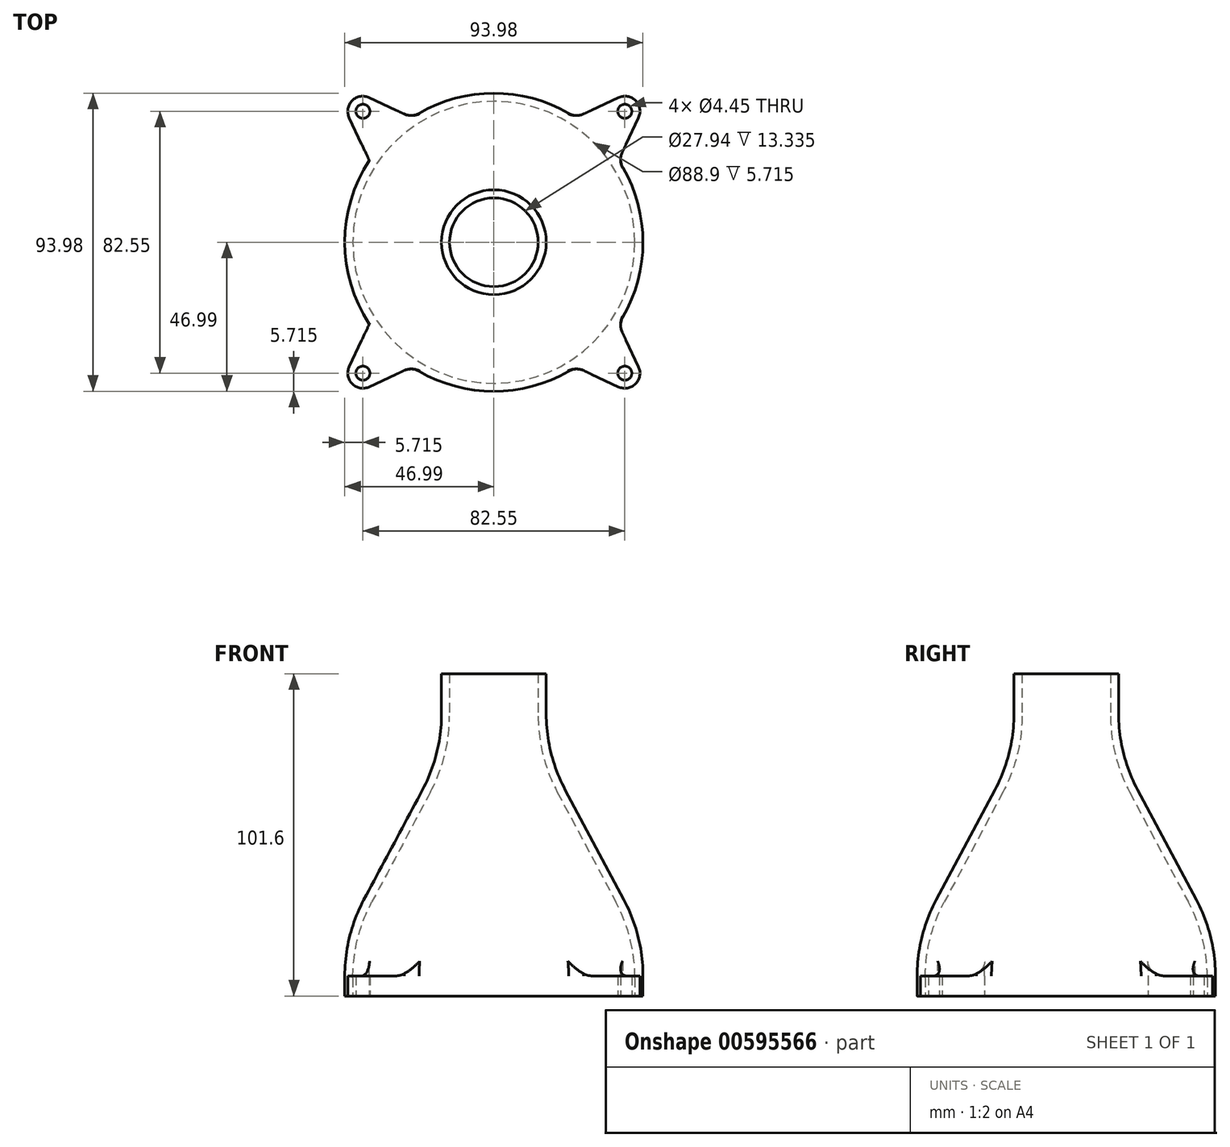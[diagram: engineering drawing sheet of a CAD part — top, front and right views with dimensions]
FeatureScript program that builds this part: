
annotation { "Feature Type Name" : "Feature", "Feature Type Description" : "" }
export const myFeature = defineFeature(function(context is Context, id is Id, definition is map)
    precondition{}
    {
        {
            var Q0;
            Q0=qCreatedBy(makeId("Front.planeOp"),FACE);
            var sketch = newSketch(context, id + "F0", { "sketchPlane" : qUnion([Q0])});
            skLineSegment(sketch, "E0", {"start": v(-66.35, 101.6) * mm, "end": v(86.52, 101.6) * mm, "construction": true});
            skLineSegment(sketch, "E1", {"start": v(0, 0) * mm, "end": v(0, 101.6) * mm, "construction": true});
            skLineSegment(sketch, "E2", {"start": v(-16.51, 101.6) * mm, "end": v(-16.51, 88.9) * mm});
            skLineSegment(sketch, "E3", {"start": v(-22.49, 65) * mm, "end": v(-41.01, 30.26) * mm});
            skLineSegment(sketch, "E4", {"start": v(-46.99, 6.35) * mm, "end": v(-46.99, 0) * mm});
            skLineSegment(sketch, "E5", {"start": v(-46.99, 0) * mm, "end": v(-44.45, 0) * mm});
            skLineSegment(sketch, "E6", {"start": v(-44.45, 0) * mm, "end": v(-44.45, 5.71) * mm});
            skLineSegment(sketch, "E7", {"start": v(-38.47, 29.62) * mm, "end": v(-19.95, 64.36) * mm});
            skLineSegment(sketch, "E8", {"start": v(-13.97, 88.27) * mm, "end": v(-13.97, 101.6) * mm});
            skLineSegment(sketch, "E9", {"start": v(-13.97, 101.6) * mm, "end": v(-16.51, 101.6) * mm});
            skPoint(sketch, "E10.visualSharp", {"position": v(-16.51, 76.2) * mm});
            skArc(sketch, "E10.filletArc", {"start": v(-22.49, 65) * mm, "mid": v(-18.03, 76.58) * mm, "end": v(-16.5, 88.9) * mm});
            skPoint(sketch, "E11.visualSharp", {"position": v(-13.97, 75.57) * mm});
            skArc(sketch, "E11.filletArc", {"start": v(-19.95, 64.36) * mm, "mid": v(-15.49, 75.94) * mm, "end": v(-13.97, 88.27) * mm});
            skPoint(sketch, "E12.visualSharp", {"position": v(-44.45, 18.42) * mm});
            skArc(sketch, "E12.filletArc", {"start": v(-38.47, 29.62) * mm, "mid": v(-42.93, 18.04) * mm, "end": v(-44.45, 5.71) * mm});
            skPoint(sketch, "E13.visualSharp", {"position": v(-47, 19.05) * mm});
            skArc(sketch, "E13.filletArc", {"start": v(-41.01, 30.26) * mm, "mid": v(-45.47, 18.67) * mm, "end": v(-46.99, 6.35) * mm});
            skSolve(sketch);
        }
        {
            var Q0;
            Q0=makeQuery(id+"F0.imprint","IMPRINT",FACE,{"disambiguationData":[TD([[makeQuery(id+"F0.imprint","IMPRINT",EDGE,{"derivedFrom":sQuery(id+"F0.wireOp",EDGE,"E2")}),1.0]])]});
            var Q1;
            Q1=sQuery(id+"F0.wireOp",EDGE,"E1");
            revolve(context, id + "F1", {"entities" : qUnion([Q0]), "axis" : qUnion([Q1]), "revolveType" : RevolveType.FULL});
        }
        {
            var Q0;
            Q0=qCreatedBy(makeId("Top.planeOp"),FACE);
            var sketch = newSketch(context, id + "F2", { "sketchPlane" : qUnion([Q0])});
            skLineSegment(sketch, "E14.bottom", {"start": v(-41.28, -41.28) * mm, "end": v(41.28, -41.28) * mm, "construction": true});
            skLineSegment(sketch, "E14.top", {"start": v(-41.27, 41.28) * mm, "end": v(41.28, 41.28) * mm, "construction": true});
            skLineSegment(sketch, "E14.left", {"start": v(-41.27, -41.28) * mm, "end": v(-41.27, 41.28) * mm, "construction": true});
            skLineSegment(sketch, "E14.right", {"start": v(41.28, -41.28) * mm, "end": v(41.28, 41.28) * mm, "construction": true});
            skLineSegment(sketch, "E15", {"start": v(-41.28, 41.28) * mm, "end": v(41.28, -41.28) * mm, "construction": true});
            skCircle(sketch, "E16", {"center": v(-41.28, -41.28) * mm, "radius": 2.22 * mm});
            skArc(sketch, "E17", {"start": v(-45.59, -39.25) * mm, "mid": v(-44.64, -44.64) * mm, "end": v(-39.25, -45.59) * mm});
            skLineSegment(sketch, "E18", {"start": v(-45.59, -39.25) * mm, "end": v(-39.27, -25.8) * mm});
            skLineSegment(sketch, "E19", {"start": v(-39.25, -45.59) * mm, "end": v(-25.8, -39.27) * mm});
            skArc(sketch, "E20.trimOffspring", {"start": v(-39.27, -25.8) * mm, "mid": v(-33.23, -33.23) * mm, "end": v(-25.8, -39.27) * mm});
            skLineSegment(sketch, "E21.1.0", {"start": v(39.25, -45.59) * mm, "end": v(25.8, -39.27) * mm});
            skCircle(sketch, "E21.1.1", {"center": v(41.28, -41.28) * mm, "radius": 2.22 * mm});
            skLineSegment(sketch, "E21.1.2", {"start": v(45.59, -39.25) * mm, "end": v(39.27, -25.8) * mm});
            skArc(sketch, "E21.1.3", {"start": v(39.25, -45.59) * mm, "mid": v(44.64, -44.64) * mm, "end": v(45.59, -39.25) * mm});
            skArc(sketch, "E21.1.4", {"start": v(25.8, -39.27) * mm, "mid": v(33.23, -33.23) * mm, "end": v(39.27, -25.8) * mm});
            skLineSegment(sketch, "E21.2.0", {"start": v(45.59, 39.25) * mm, "end": v(39.27, 25.8) * mm});
            skCircle(sketch, "E21.2.1", {"center": v(41.28, 41.27) * mm, "radius": 2.22 * mm});
            skLineSegment(sketch, "E21.2.2", {"start": v(39.25, 45.59) * mm, "end": v(25.8, 39.27) * mm});
            skArc(sketch, "E21.2.3", {"start": v(45.59, 39.25) * mm, "mid": v(44.64, 44.64) * mm, "end": v(39.25, 45.59) * mm});
            skArc(sketch, "E21.2.4", {"start": v(39.27, 25.8) * mm, "mid": v(33.23, 33.23) * mm, "end": v(25.8, 39.27) * mm});
            skLineSegment(sketch, "E21.3.0", {"start": v(-39.25, 45.59) * mm, "end": v(-25.8, 39.27) * mm});
            skCircle(sketch, "E21.3.1", {"center": v(-41.27, 41.28) * mm, "radius": 2.22 * mm});
            skLineSegment(sketch, "E21.3.2", {"start": v(-45.59, 39.25) * mm, "end": v(-39.27, 25.8) * mm});
            skArc(sketch, "E21.3.3", {"start": v(-39.25, 45.59) * mm, "mid": v(-44.64, 44.64) * mm, "end": v(-45.59, 39.25) * mm});
            skArc(sketch, "E21.3.4", {"start": v(-25.8, 39.27) * mm, "mid": v(-33.23, 33.23) * mm, "end": v(-39.27, 25.8) * mm});
            skSolve(sketch);
        }
        {
            var Q0;
            Q0=makeQuery(id+"F2.imprint","IMPRINT",FACE,{"disambiguationData":[TD([[makeQuery(id+"F2.imprint","IMPRINT",EDGE,{"derivedFrom":sQuery(id+"F2.wireOp",EDGE,"E16")}),-1.0]])]});
            var Q1;
            Q1=makeQuery(id+"F2.imprint","IMPRINT",FACE,{"disambiguationData":[TD([[makeQuery(id+"F2.imprint","IMPRINT",EDGE,{"derivedFrom":sQuery(id+"F2.wireOp",EDGE,"E21.1.0")}),-1.0]])]});
            var Q2;
            Q2=makeQuery(id+"F2.imprint","IMPRINT",FACE,{"disambiguationData":[TD([[makeQuery(id+"F2.imprint","IMPRINT",EDGE,{"derivedFrom":sQuery(id+"F2.wireOp",EDGE,"E21.2.0")}),-1.0]])]});
            var Q3;
            Q3=makeQuery(id+"F2.imprint","IMPRINT",FACE,{"disambiguationData":[TD([[makeQuery(id+"F2.imprint","IMPRINT",EDGE,{"derivedFrom":sQuery(id+"F2.wireOp",EDGE,"E21.3.0")}),-1.0]])]});
            extrude(context, id + "F3", {"entities" : qUnion([Q0, Q1, Q2, Q3]), "operationType" : NewBodyOperationType.ADD, "depth" : 6.35 * mm, "offsetDistance" : 25.4 * mm});
        }
        {
            var Q0;
            Q0=makeQuery(id+"F3.boolean.opBoolean","MERGE",EDGE,{"derivedFrom":[makeQuery(id+"F1.opRevolve","SWEPT_EDGE",EDGE,{"disambiguationData":[OSD([sQuery(id+"F0.wireOp",EDGE,"E4"),sQuery(id+"F0.wireOp",EDGE,"E13.filletArc")])]}),makeQuery(id+"F3.opExtrude","CAP_EDGE",EDGE,{"disambiguationData":[OSD([sQuery(id+"F2.wireOp",EDGE,"E20.trimOffspring")])],"isStart":false})]});
            var Q1;
            Q1=makeQuery(id+"F3.opExtrude","SWEPT_EDGE",EDGE,{"disambiguationData":[OSD([sQuery(id+"F2.wireOp",EDGE,"E19"),sQuery(id+"F2.wireOp",EDGE,"E20.trimOffspring")])]});
            var Q2;
            Q2=makeQuery(id+"F3.opExtrude","SWEPT_EDGE",EDGE,{"disambiguationData":[OSD([sQuery(id+"F2.wireOp",EDGE,"E18"),sQuery(id+"F2.wireOp",EDGE,"E20.trimOffspring")])]});
            var Q3;
            Q3=makeQuery(id+"F3.boolean.opBoolean","MERGE",EDGE,{"derivedFrom":[makeQuery(id+"F1.opRevolve","SWEPT_EDGE",EDGE,{"disambiguationData":[OSD([sQuery(id+"F0.wireOp",EDGE,"E4"),sQuery(id+"F0.wireOp",EDGE,"E13.filletArc")])]}),makeQuery(id+"F3.opExtrude","CAP_EDGE",EDGE,{"disambiguationData":[OSD([sQuery(id+"F2.wireOp",EDGE,"E21.3.4")])],"isStart":false})]});
            var Q4;
            Q4=makeQuery(id+"F3.opExtrude","SWEPT_EDGE",EDGE,{"disambiguationData":[OSD([sQuery(id+"F2.wireOp",EDGE,"E21.3.2"),sQuery(id+"F2.wireOp",EDGE,"E21.3.4")])]});
            var Q5;
            Q5=makeQuery(id+"F3.opExtrude","SWEPT_EDGE",EDGE,{"disambiguationData":[OSD([sQuery(id+"F2.wireOp",EDGE,"E21.3.0"),sQuery(id+"F2.wireOp",EDGE,"E21.3.4")])]});
            var Q6;
            Q6=makeQuery(id+"F3.opExtrude","SWEPT_EDGE",EDGE,{"disambiguationData":[OSD([sQuery(id+"F2.wireOp",EDGE,"E21.2.2"),sQuery(id+"F2.wireOp",EDGE,"E21.2.4")])]});
            var Q7;
            Q7=makeQuery(id+"F3.boolean.opBoolean","MERGE",EDGE,{"derivedFrom":[makeQuery(id+"F1.opRevolve","SWEPT_EDGE",EDGE,{"disambiguationData":[OSD([sQuery(id+"F0.wireOp",EDGE,"E4"),sQuery(id+"F0.wireOp",EDGE,"E13.filletArc")])]}),makeQuery(id+"F3.opExtrude","CAP_EDGE",EDGE,{"disambiguationData":[OSD([sQuery(id+"F2.wireOp",EDGE,"E21.2.4")])],"isStart":false})]});
            var Q8;
            Q8=makeQuery(id+"F3.opExtrude","SWEPT_EDGE",EDGE,{"disambiguationData":[OSD([sQuery(id+"F2.wireOp",EDGE,"E21.2.0"),sQuery(id+"F2.wireOp",EDGE,"E21.2.4")])]});
            var Q9;
            Q9=makeQuery(id+"F3.boolean.opBoolean","MERGE",EDGE,{"derivedFrom":[makeQuery(id+"F1.opRevolve","SWEPT_EDGE",EDGE,{"disambiguationData":[OSD([sQuery(id+"F0.wireOp",EDGE,"E4"),sQuery(id+"F0.wireOp",EDGE,"E13.filletArc")])]}),makeQuery(id+"F3.opExtrude","CAP_EDGE",EDGE,{"disambiguationData":[OSD([sQuery(id+"F2.wireOp",EDGE,"E21.1.4")])],"isStart":false})]});
            var Q10;
            Q10=makeQuery(id+"F3.opExtrude","SWEPT_EDGE",EDGE,{"disambiguationData":[OSD([sQuery(id+"F2.wireOp",EDGE,"E21.1.2"),sQuery(id+"F2.wireOp",EDGE,"E21.1.4")])]});
            var Q11;
            Q11=makeQuery(id+"F3.opExtrude","SWEPT_EDGE",EDGE,{"disambiguationData":[OSD([sQuery(id+"F2.wireOp",EDGE,"E21.1.0"),sQuery(id+"F2.wireOp",EDGE,"E21.1.4")])]});
            fillet(context, id + "F4", {"entities" : qUnion([Q0, Q1, Q2, Q3, Q4, Q5, Q6, Q7, Q8, Q9, Q10, Q11]), "radius" : 5.08 * mm, "tangentPropagation" : true, "allowEdgeOverflow" : false});
        }
    });
